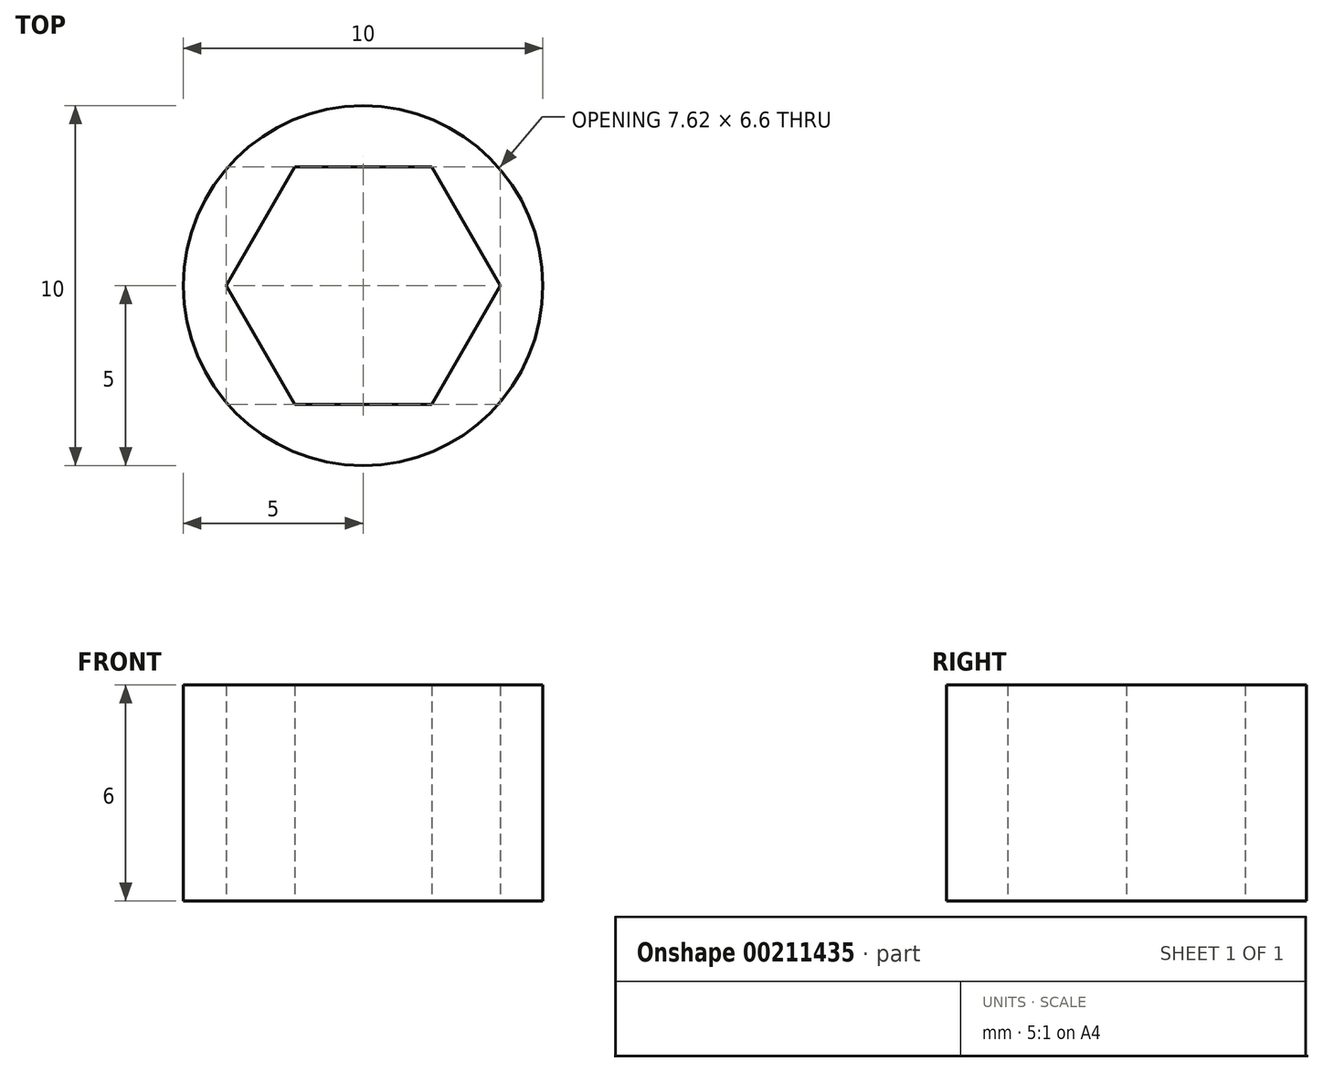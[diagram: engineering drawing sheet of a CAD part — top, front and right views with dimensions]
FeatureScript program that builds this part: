
annotation { "Feature Type Name" : "Feature", "Feature Type Description" : "" }
export const myFeature = defineFeature(function(context is Context, id is Id, definition is map)
    precondition{}
    {
        {
            var Q0;
            Q0=qCreatedBy(makeId("Top.planeOp"),FACE);
            var sketch = newSketch(context, id + "F0", { "sketchPlane" : qUnion([Q0])});
            skCircle(sketch, "E0", {"center": v(0, 0) * mm, "radius": 5 * mm});
            skCircle(sketch, "E1.cCircle", {"center": v(0, 0) * mm, "radius": 3.3 * mm, "construction": true});
            skLineSegment(sketch, "E1.0", {"start": v(-1.9, 3.3) * mm, "end": v(1.9, 3.3) * mm});
            skLineSegment(sketch, "E1.1", {"start": v(1.9, 3.3) * mm, "end": v(3.81, 0) * mm});
            skLineSegment(sketch, "E1.2", {"start": v(3.81, 0) * mm, "end": v(1.9, -3.3) * mm});
            skLineSegment(sketch, "E1.3", {"start": v(1.9, -3.3) * mm, "end": v(-1.9, -3.3) * mm});
            skLineSegment(sketch, "E1.4", {"start": v(-1.9, -3.3) * mm, "end": v(-3.81, 0) * mm});
            skLineSegment(sketch, "E1.5", {"start": v(-3.81, 0) * mm, "end": v(-1.9, 3.3) * mm});
            skPoint(sketch, "E1.0.midPoint", {"position": v(0, 3.3) * mm});
            skSolve(sketch);
        }
        {
            var Q0;
            Q0=makeQuery(id+"F0.imprint","IMPRINT",FACE,{"disambiguationData":[TD([[makeQuery(id+"F0.imprint","IMPRINT",EDGE,{"derivedFrom":sQuery(id+"F0.wireOp",EDGE,"E0")}),1.0]])]});
            extrude(context, id + "F1", {"entities" : qUnion([Q0]), "depth" : 6 * mm});
        }
    });
